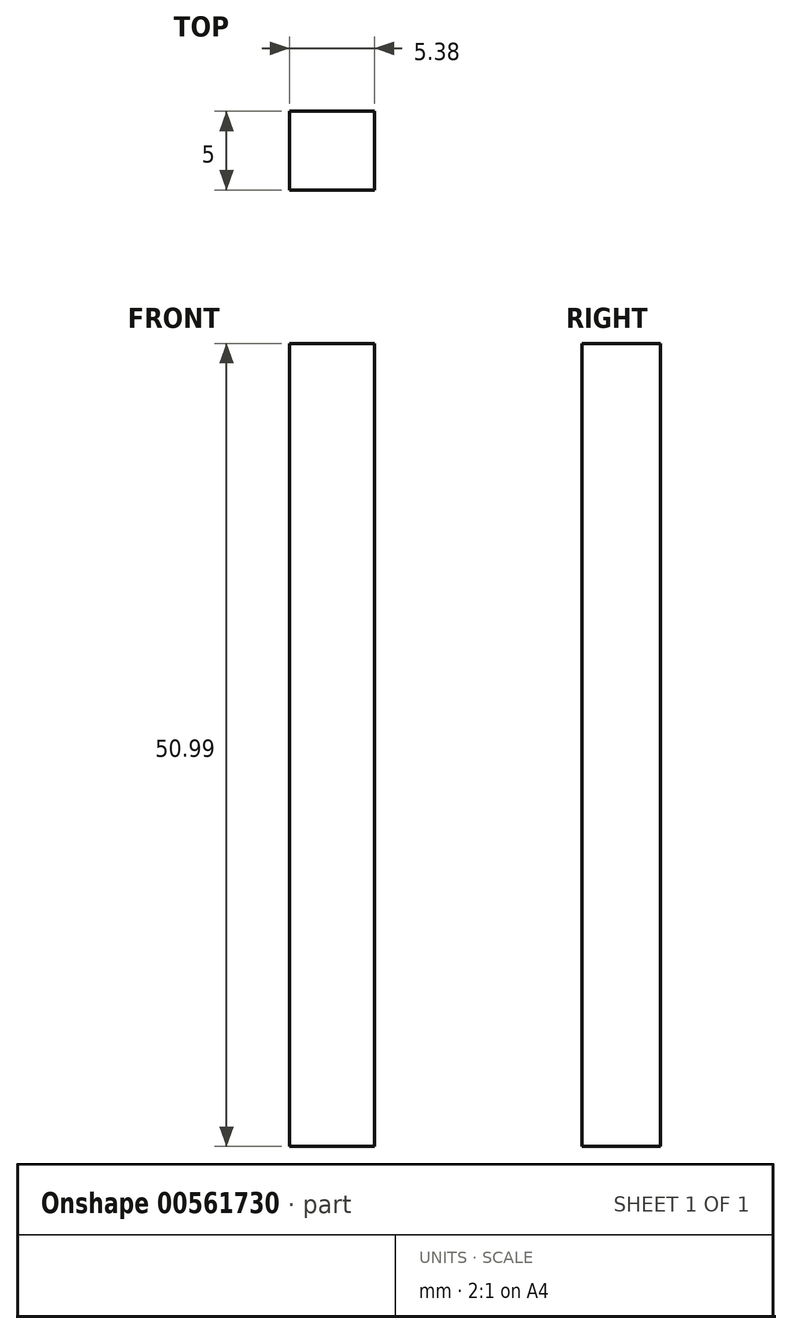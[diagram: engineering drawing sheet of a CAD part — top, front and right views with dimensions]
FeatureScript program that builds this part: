
annotation { "Feature Type Name" : "Feature", "Feature Type Description" : "" }
export const myFeature = defineFeature(function(context is Context, id is Id, definition is map)
    precondition{}
    {
        {
            var Q0;
            Q0=qCreatedBy(makeId("Front.planeOp"),FACE);
            var sketch = newSketch(context, id + "F0", { "sketchPlane" : qUnion([Q0])});
            skLineSegment(sketch, "E0", {"start": v(-44.9, 17.42) * mm, "end": v(-44.9, -33.57) * mm});
            skLineSegment(sketch, "E1", {"start": v(-44.9, -33.57) * mm, "end": v(-39.52, -33.57) * mm});
            skLineSegment(sketch, "E2", {"start": v(-39.52, -33.57) * mm, "end": v(-39.52, 17.42) * mm});
            skLineSegment(sketch, "E3", {"start": v(-39.52, 17.42) * mm, "end": v(-44.9, 17.42) * mm});
            skSolve(sketch);
        }
        {
            var Q0;
            Q0=makeQuery(id+"F0.imprint","IMPRINT",FACE,{"disambiguationData":[TD([[makeQuery(id+"F0.imprint","IMPRINT",EDGE,{"derivedFrom":sQuery(id+"F0.wireOp",EDGE,"E0")}),1.0]])]});
            extrude(context, id + "F1", {"entities" : qUnion([Q0]), "depth" : 5 * mm, "offsetDistance" : 25 * mm});
        }
    });
